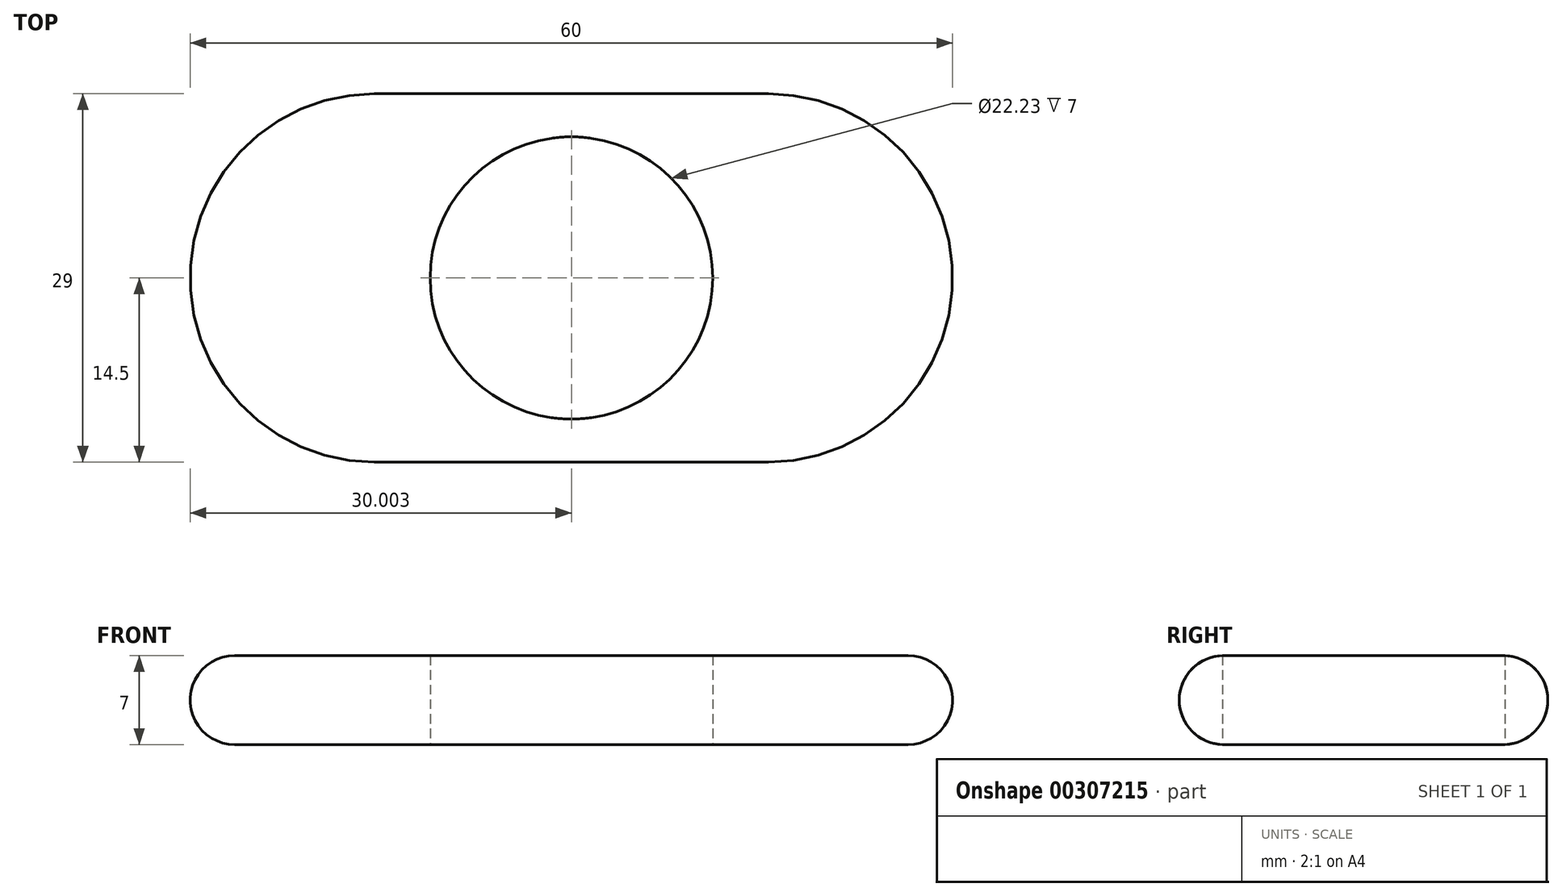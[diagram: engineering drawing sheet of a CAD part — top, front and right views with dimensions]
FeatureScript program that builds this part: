
annotation { "Feature Type Name" : "Feature", "Feature Type Description" : "" }
export const myFeature = defineFeature(function(context is Context, id is Id, definition is map)
    precondition{}
    {
        {
            var Q0;
            Q0=qCreatedBy(makeId("Top.planeOp"),FACE);
            var sketch = newSketch(context, id + "F0", { "sketchPlane" : qUnion([Q0])});
            skLineSegment(sketch, "E0.bottom", {"start": v(-5.84, 14.5) * mm, "end": v(25.16, 14.5) * mm});
            skLineSegment(sketch, "E0.top", {"start": v(-5.84, -14.5) * mm, "end": v(25.16, -14.5) * mm});
            skLineSegment(sketch, "E0.left", {"start": v(-20.34, 0) * mm, "end": v(-20.34, 0) * mm});
            skLineSegment(sketch, "E0.right", {"start": v(39.66, 0) * mm, "end": v(39.66, 0) * mm});
            skPoint(sketch, "E1.visualSharp", {"position": v(-20.34, 14.5) * mm});
            skArc(sketch, "E1.filletArc", {"start": v(-5.84, 14.5) * mm, "mid": v(-16.09, 10.25) * mm, "end": v(-20.34, 0) * mm});
            skPoint(sketch, "E2.visualSharp", {"position": v(-20.34, -14.5) * mm});
            skArc(sketch, "E2.filletArc", {"start": v(-20.34, 0) * mm, "mid": v(-16.09, -10.25) * mm, "end": v(-5.84, -14.5) * mm});
            skPoint(sketch, "E3.visualSharp", {"position": v(39.66, -14.5) * mm});
            skArc(sketch, "E3.filletArc", {"start": v(25.16, -14.5) * mm, "mid": v(35.42, -10.25) * mm, "end": v(39.66, 0) * mm});
            skPoint(sketch, "E4.visualSharp", {"position": v(39.66, 14.5) * mm});
            skArc(sketch, "E4.filletArc", {"start": v(39.66, 0) * mm, "mid": v(35.42, 10.25) * mm, "end": v(25.16, 14.5) * mm});
            skPoint(sketch, "E5", {"position": v(9.66, 14.5) * mm});
            skPoint(sketch, "E6", {"position": v(9.66, -14.5) * mm});
            skPoint(sketch, "E7", {"position": v(-20.34, 0) * mm});
            skPoint(sketch, "E8", {"position": v(39.66, 0) * mm});
            skCircle(sketch, "E9", {"center": v(9.66, 0) * mm, "radius": 11.11 * mm});
            skSolve(sketch);
        }
        {
            var Q0;
            Q0=makeQuery(id+"F0.imprint","IMPRINT",FACE,{"disambiguationData":[TD([[makeQuery(id+"F0.imprint","IMPRINT",EDGE,{"derivedFrom":sQuery(id+"F0.wireOp",EDGE,"E0.bottom")}),-1.0]])]});
            extrude(context, id + "F1", {"entities" : qUnion([Q0]), "depth" : 7 * mm});
        }
        {
            var Q0;
            Q0=makeQuery(id+"F1.opExtrude","CAP_EDGE",EDGE,{"disambiguationData":[OSD([sQuery(id+"F0.wireOp",EDGE,"E1.filletArc"),sQuery(id+"F0.wireOp",EDGE,"E2.filletArc")])],"isStart":false});
            var Q1;
            Q1=makeQuery(id+"F1.opExtrude","CAP_EDGE",EDGE,{"disambiguationData":[OSD([sQuery(id+"F0.wireOp",EDGE,"E3.filletArc"),sQuery(id+"F0.wireOp",EDGE,"E4.filletArc")])],"isStart":true});
            fillet(context, id + "F2", {"entities" : qUnion([Q0, Q1]), "radius" : 3.5 * mm, "tangentPropagation" : true, "allowEdgeOverflow" : false});
        }
    });
